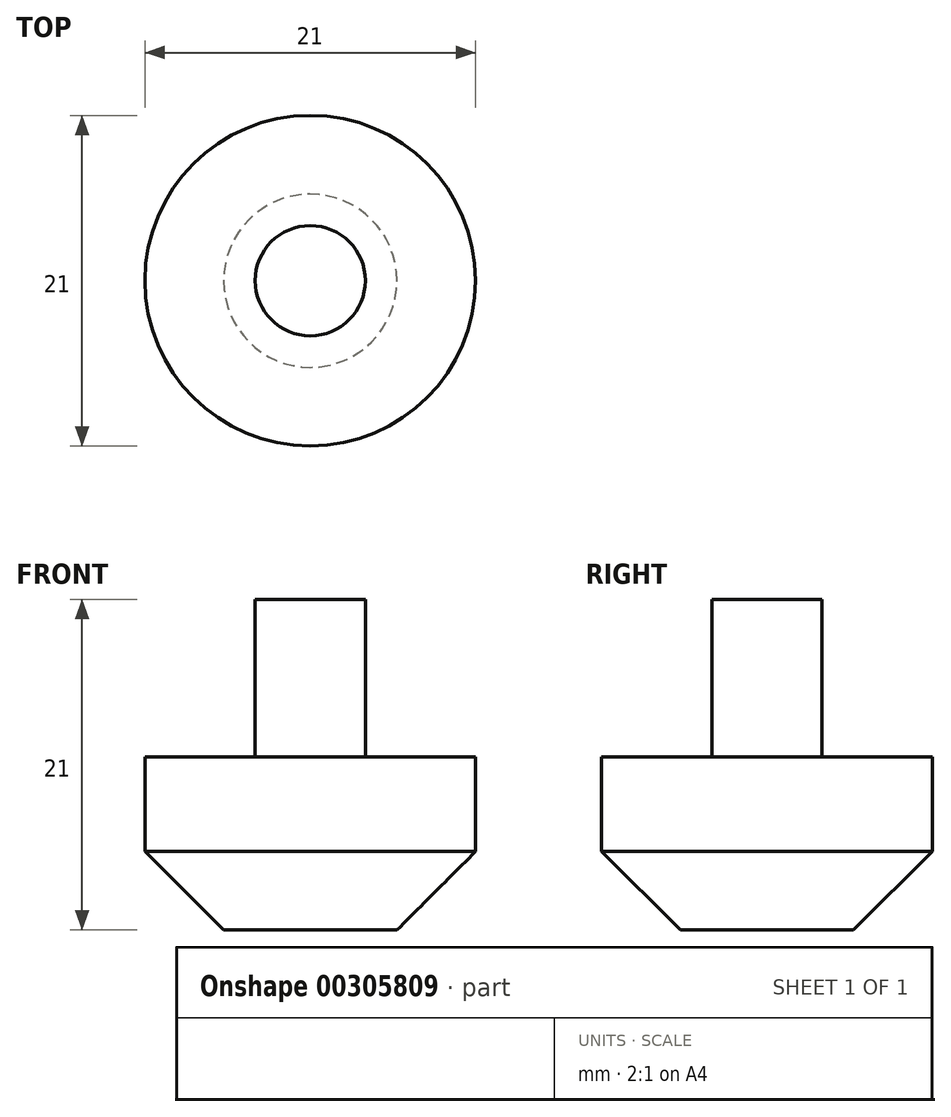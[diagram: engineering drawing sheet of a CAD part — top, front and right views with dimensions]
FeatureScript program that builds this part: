
annotation { "Feature Type Name" : "Feature", "Feature Type Description" : "" }
export const myFeature = defineFeature(function(context is Context, id is Id, definition is map)
    precondition{}
    {
        {
            var Q0;
            Q0=qCreatedBy(makeId("Top.planeOp"),FACE);
            var sketch = newSketch(context, id + "F0", { "sketchPlane" : qUnion([Q0])});
            skCircle(sketch, "E0", {"center": v(0, 0) * mm, "radius": 10.5 * mm});
            skSolve(sketch);
        }
        {
            var Q0;
            Q0 = qSketchRegion(id + "F0", true);
            extrude(context, id + "F1", {"entities" : qUnion([Q0]), "depth" : 11 * mm});
        }
        {
            var Q0;
            Q0=makeQuery(id+"F1.opExtrude","CAP_FACE",FACE,{"disambiguationData":[OSD([sQuery(id+"F0.wireOp",EDGE,"E0")])],"isStart":false});
            var sketch = newSketch(context, id + "F2", { "sketchPlane" : qUnion([Q0])});
            skCircle(sketch, "E1", {"center": v(0, 0) * mm, "radius": 3.5 * mm});
            skSolve(sketch);
        }
        {
            var Q0;
            Q0 = qSketchRegion(id + "F2", true);
            extrude(context, id + "F3", {"entities" : qUnion([Q0]), "operationType" : NewBodyOperationType.ADD, "depth" : 10 * mm});
        }
        {
            var Q0;
            Q0=makeQuery(id+"F1.opExtrude","CAP_EDGE",EDGE,{"disambiguationData":[OSD([sQuery(id+"F0.wireOp",EDGE,"E0")])],"isStart":true});
            chamfer(context, id + "F4", {"entities" : qUnion([Q0]), "width" : 5 * mm, "tangentPropagation" : true});
        }
    });
